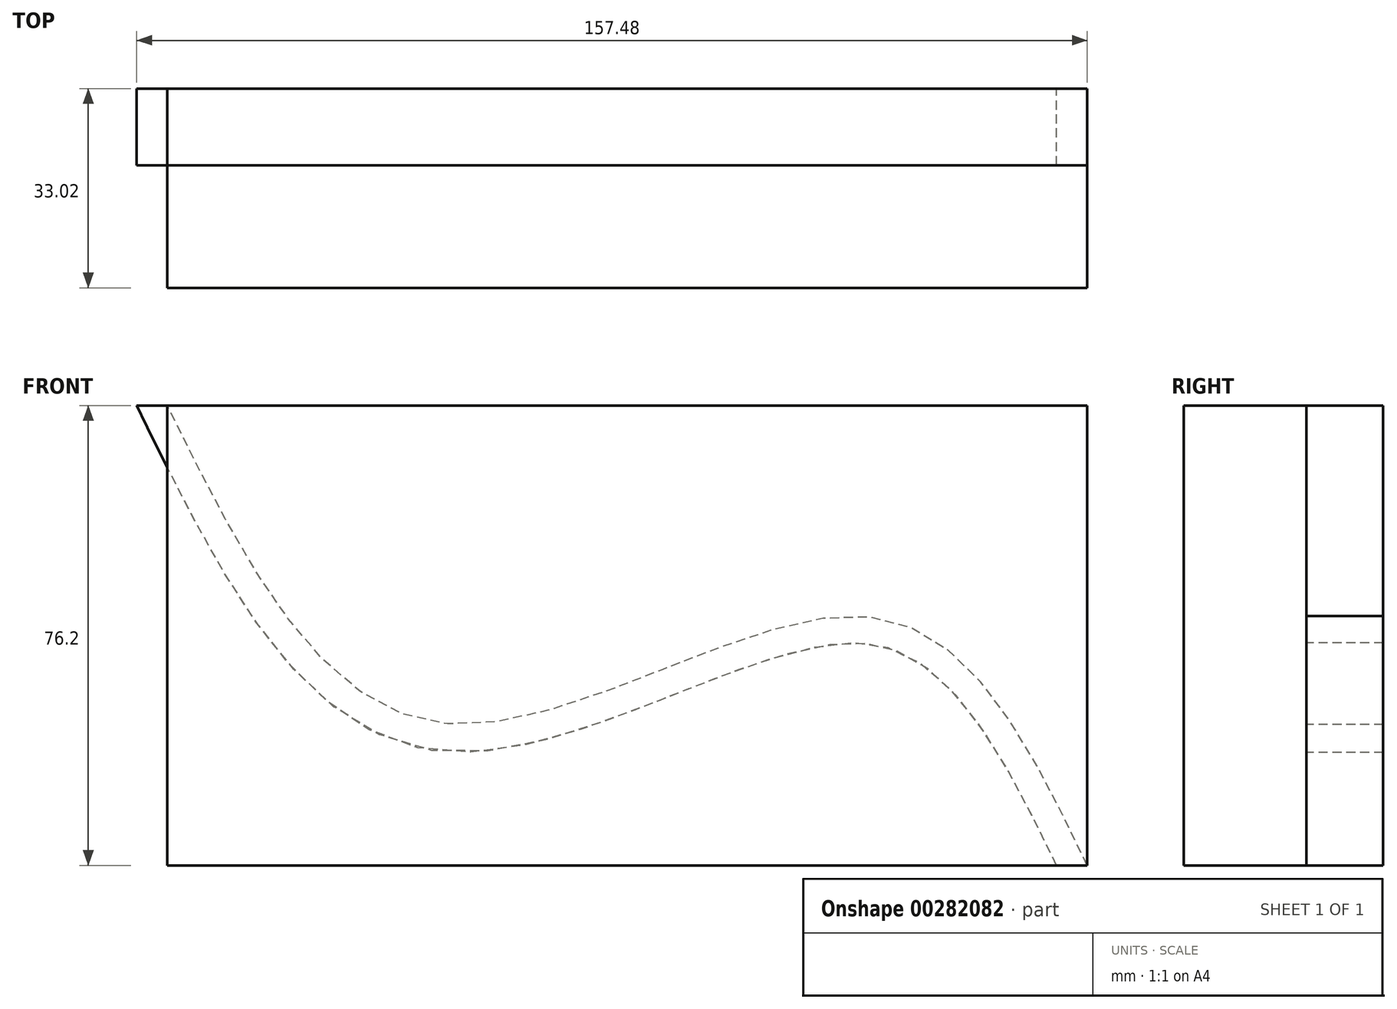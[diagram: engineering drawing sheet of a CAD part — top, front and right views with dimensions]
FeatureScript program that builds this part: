
annotation { "Feature Type Name" : "Feature", "Feature Type Description" : "" }
export const myFeature = defineFeature(function(context is Context, id is Id, definition is map)
    precondition{}
    {
        {
            var Q0;
            Q0=qCreatedBy(makeId("Front.planeOp"),FACE);
            var sketch = newSketch(context, id + "F0", { "sketchPlane" : qUnion([Q0])});
            skLineSegment(sketch, "E0.bottom", {"start": v(0, 0) * mm, "end": v(-152.4, 0) * mm});
            skLineSegment(sketch, "E0.top", {"start": v(0, 76.2) * mm, "end": v(-152.4, 76.2) * mm});
            skLineSegment(sketch, "E0.left", {"start": v(0, 0) * mm, "end": v(0, 76.2) * mm});
            skLineSegment(sketch, "E0.right", {"start": v(-152.4, 0) * mm, "end": v(-152.4, 76.2) * mm});
            skFitSpline(sketch, "E1", {"points": [v(0, 0) * mm, v(-36.08, 41.17) * mm, v(-106.73, 23.5) * mm, v(-152.4, 76.2) * mm], "startDerivative": vector(-93.53, 194.1) * mm, "endDerivative": vector(-108.84, 220.38) * mm});
            skSolve(sketch);
        }
        {
            var Q0;
            Q0=qCreatedBy(makeId("Top.planeOp"),FACE);
            var sketch = newSketch(context, id + "F1", { "sketchPlane" : qUnion([Q0])});
            skLineSegment(sketch, "E2.bottom", {"start": v(0, 0) * mm, "end": v(-5.08, 0) * mm});
            skLineSegment(sketch, "E2.top", {"start": v(0, 12.7) * mm, "end": v(-5.08, 12.7) * mm});
            skLineSegment(sketch, "E2.left", {"start": v(0, 0) * mm, "end": v(0, 12.7) * mm});
            skLineSegment(sketch, "E2.right", {"start": v(-5.08, 0) * mm, "end": v(-5.08, 12.7) * mm});
            skSolve(sketch);
        }
        {
            var Q0;
            Q0=makeQuery(id+"F1.imprint","IMPRINT",FACE,{"disambiguationData":[TD([[makeQuery(id+"F1.imprint","IMPRINT",EDGE,{"derivedFrom":sQuery(id+"F1.wireOp",EDGE,"E2.bottom")}),-1.0]])]});
            var Q1;
            Q1=sQuery(id+"F0.wireOp",EDGE,"E1");
            sweep(context, id + "F2", {"profiles" : qUnion([Q0]), "path" : qUnion([Q1])});
        }
        {
            var Q0;
            Q0=makeQuery(id+"F0.imprint","IMPRINT",FACE,{"disambiguationData":[TD([[makeQuery(id+"F0.imprint","IMPRINT",EDGE,{"derivedFrom":sQuery(id+"F0.wireOp",EDGE,"E0.top")}),1.0]])]});
            var Q1;
            Q1=makeQuery(id+"F0.imprint","IMPRINT",FACE,{"disambiguationData":[TD([[makeQuery(id+"F0.imprint","IMPRINT",EDGE,{"derivedFrom":sQuery(id+"F0.wireOp",EDGE,"E0.bottom")}),-1.0]])]});
            extrude(context, id + "F3", {"entities" : qUnion([Q0, Q1]), "operationType" : NewBodyOperationType.ADD, "depth" : 20.32 * mm});
        }
    });
